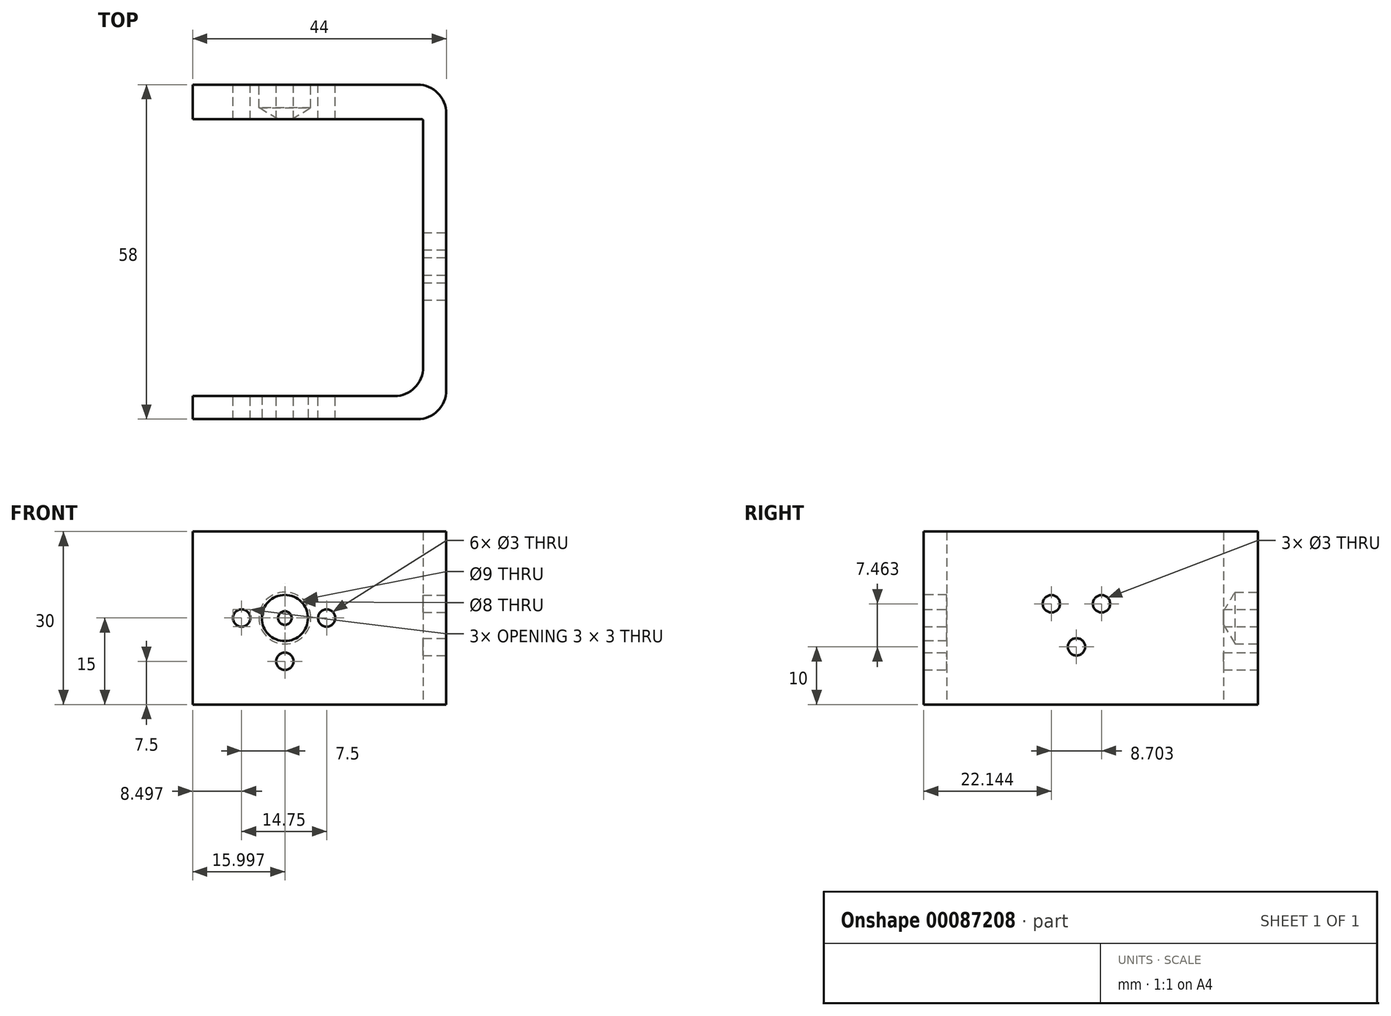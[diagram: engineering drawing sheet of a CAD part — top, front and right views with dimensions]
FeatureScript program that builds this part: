
annotation { "Feature Type Name" : "Feature", "Feature Type Description" : "" }
export const myFeature = defineFeature(function(context is Context, id is Id, definition is map)
    precondition{}
    {
        {
            var Q0;
            Q0=qCreatedBy(makeId("Top.planeOp"),FACE);
            var sketch = newSketch(context, id + "F0", { "sketchPlane" : qUnion([Q0])});
            skLineSegment(sketch, "E0", {"start": v(-0.12, 52.66) * mm, "end": v(-0.12, 9.9) * mm});
            skLineSegment(sketch, "E1", {"start": v(-5.12, 4.9) * mm, "end": v(-40.12, 4.9) * mm});
            skLineSegment(sketch, "E2", {"start": v(-0.37, 52.9) * mm, "end": v(-40.12, 52.9) * mm});
            skLineSegment(sketch, "E3", {"start": v(-40.12, 4.9) * mm, "end": v(-40.12, 0.9) * mm});
            skLineSegment(sketch, "E4", {"start": v(-40.12, 58.9) * mm, "end": v(-40.12, 52.9) * mm});
            skPoint(sketch, "E5.0.end.orphan", {"position": v(3.88, 4.9) * mm});
            skPoint(sketch, "E5.0.start.orphan", {"position": v(3.88, 54.9) * mm});
            skLineSegment(sketch, "E6", {"start": v(3.88, 53.9) * mm, "end": v(3.88, 5.9) * mm});
            skLineSegment(sketch, "E7", {"start": v(-40.12, 58.9) * mm, "end": v(-1.12, 58.9) * mm});
            skLineSegment(sketch, "E8", {"start": v(-1.12, 0.9) * mm, "end": v(-40.12, 0.9) * mm});
            skPoint(sketch, "E9.visualSharp", {"position": v(3.88, 58.9) * mm});
            skArc(sketch, "E9.filletArc", {"start": v(3.88, 53.9) * mm, "mid": v(2.41, 57.44) * mm, "end": v(-1.12, 58.9) * mm});
            skPoint(sketch, "E10.visualSharp", {"position": v(-0.12, 52.9) * mm});
            skArc(sketch, "E10.filletArc", {"start": v(-0.12, 52.66) * mm, "mid": v(-0.2, 52.83) * mm, "end": v(-0.37, 52.9) * mm});
            skPoint(sketch, "E11.visualSharp", {"position": v(-0.12, 4.9) * mm});
            skLineSegment(sketch, "E11.filletArc", {"start": v(-0.12, 4.9) * mm, "end": v(-0.12, 4.9) * mm});
            skPoint(sketch, "E12.visualSharp", {"position": v(3.88, 0.9) * mm});
            skArc(sketch, "E12.filletArc", {"start": v(-1.12, 0.9) * mm, "mid": v(2.41, 2.37) * mm, "end": v(3.88, 5.9) * mm});
            skArc(sketch, "E13.filletArc", {"start": v(-5.12, 4.9) * mm, "mid": v(-1.59, 6.37) * mm, "end": v(-0.12, 9.9) * mm});
            skSolve(sketch);
        }
        {
            var Q0;
            Q0 = qSketchRegion(id + "F0", true);
            extrude(context, id + "F1", {"entities" : qUnion([Q0]), "depth" : 30 * mm});
        }
        {
            var Q0;
            Q0=makeQuery(id+"F1.opExtrude","SWEPT_FACE",FACE,{"disambiguationData":[OSD([sQuery(id+"F0.wireOp",EDGE,"E6")])]});
            var sketch = newSketch(context, id + "F2", { "sketchPlane" : qUnion([Q0])});
            skCircle(sketch, "E14", {"center": v(23.05, 17.46) * mm, "radius": 1.5 * mm});
            skCircle(sketch, "E15", {"center": v(27.4, 10) * mm, "radius": 1.5 * mm});
            skCircle(sketch, "E16", {"center": v(31.76, 17.46) * mm, "radius": 1.5 * mm});
            skPoint(sketch, "E17.orphan", {"position": v(0.9, 15) * mm});
            skPoint(sketch, "E18.orphan", {"position": v(0.9, 0) * mm});
            skPoint(sketch, "E19.orphan", {"position": v(29.9, 0) * mm});
            skPoint(sketch, "E20.orphan", {"position": v(53.9, 15) * mm});
            skPoint(sketch, "E21.orphan", {"position": v(53.9, 30) * mm});
            skPoint(sketch, "E22.orphan", {"position": v(29.9, 30) * mm});
            skPoint(sketch, "E23.center.orphan", {"position": v(27.4, 15) * mm});
            skSolve(sketch);
        }
        {
            var Q0;
            Q0=sQuery(id+"F2.wireOp",VERTEX,"E14.center");
            var Q1;
            Q1=sQuery(id+"F2.wireOp",VERTEX,"E15.center");
            var Q2;
            Q2=sQuery(id+"F2.wireOp",VERTEX,"E16.center");
            var Q3;
            Q3=makeQuery(id+"F1.opExtrude","SWEPT_BODY",BODY,{"disambiguationData":[OSD([sQuery(id+"F0.wireOp",EDGE,"E0"),sQuery(id+"F0.wireOp",EDGE,"E1"),sQuery(id+"F0.wireOp",EDGE,"E2"),sQuery(id+"F0.wireOp",EDGE,"E3"),sQuery(id+"F0.wireOp",EDGE,"E4"),sQuery(id+"F0.wireOp",EDGE,"E6"),sQuery(id+"F0.wireOp",EDGE,"E7"),sQuery(id+"F0.wireOp",EDGE,"E8"),sQuery(id+"F0.wireOp",EDGE,"E9.filletArc"),sQuery(id+"F0.wireOp",EDGE,"E10.filletArc"),sQuery(id+"F0.wireOp",EDGE,"E11.filletArc")])]});
            hole(context, id + "F3", {"style" : HoleStyle.SIMPLE, "endStyle" : HoleEndStyle.THROUGH, "holeDiameter" : 3 * mm, "locations" : qUnion([Q0, Q1, Q2]), "scope" : qUnion([Q3]), "isTappedThrough" : true});
        }
        {
            var Q0;
            Q0=makeQuery(id+"F1.opExtrude","SWEPT_FACE",FACE,{"disambiguationData":[OSD([sQuery(id+"F0.wireOp",EDGE,"E7")])]});
            var sketch = newSketch(context, id + "F4", { "sketchPlane" : qUnion([Q0])});
            skCircle(sketch, "E24", {"center": v(24.12, 15) * mm, "radius": 4.5 * mm});
            skCircle(sketch, "E25", {"center": v(24.12, 22.5) * mm, "radius": 1.5 * mm});
            skCircle(sketch, "E26", {"center": v(16.87, 15) * mm, "radius": 1.5 * mm});
            skCircle(sketch, "E27", {"center": v(24.12, 7.5) * mm, "radius": 1.5 * mm});
            skCircle(sketch, "E28", {"center": v(31.62, 15) * mm, "radius": 1.5 * mm});
            skSolve(sketch);
        }
        {
            var Q0;
            Q0=sQuery(id+"F4.wireOp",VERTEX,"E24.center");
            var Q1;
            Q1=makeQuery(id+"F1.opExtrude","SWEPT_BODY",BODY,{"disambiguationData":[OSD([sQuery(id+"F0.wireOp",EDGE,"E0"),sQuery(id+"F0.wireOp",EDGE,"E1"),sQuery(id+"F0.wireOp",EDGE,"E2"),sQuery(id+"F0.wireOp",EDGE,"E3"),sQuery(id+"F0.wireOp",EDGE,"E4"),sQuery(id+"F0.wireOp",EDGE,"E6"),sQuery(id+"F0.wireOp",EDGE,"E7"),sQuery(id+"F0.wireOp",EDGE,"E8"),sQuery(id+"F0.wireOp",EDGE,"E9.filletArc"),sQuery(id+"F0.wireOp",EDGE,"E10.filletArc")])]});
            hole(context, id + "F5", {"style" : HoleStyle.SIMPLE, "endStyle" : HoleEndStyle.BLIND, "holeDiameter" : 9 * mm, "holeDepth" : 4 * mm, "startFromSketch" : true, "locations" : qUnion([Q0]), "scope" : qUnion([Q1])});
        }
        {
            var Q0;
            Q0=makeQuery(id+"F1.opExtrude","SWEPT_FACE",FACE,{"disambiguationData":[OSD([sQuery(id+"F0.wireOp",EDGE,"E7")])]});
            var sketch = newSketch(context, id + "F6", { "sketchPlane" : qUnion([Q0])});
            skCircle(sketch, "E29", {"center": v(24.12, 15) * mm, "radius": 4.5 * mm});
            skPoint(sketch, "E30.trimOffspring.end.orphan", {"position": v(31.62, 15) * mm});
            skPoint(sketch, "E31.start.orphan", {"position": v(24.12, 7.5) * mm});
            skPoint(sketch, "E32.orphan", {"position": v(16.87, 15) * mm});
            skSolve(sketch);
        }
        {
            var Q0;
            Q0=sQuery(id+"F6.wireOp",VERTEX,"E30.trimOffspring.end.orphan");
            var Q1;
            Q1=sQuery(id+"F6.wireOp",VERTEX,"E31.start.orphan");
            var Q2;
            Q2=sQuery(id+"F6.wireOp",VERTEX,"E32.orphan");
            var Q3;
            Q3=makeQuery(id+"F1.opExtrude","SWEPT_BODY",BODY,{"disambiguationData":[OSD([sQuery(id+"F0.wireOp",EDGE,"E0"),sQuery(id+"F0.wireOp",EDGE,"E1"),sQuery(id+"F0.wireOp",EDGE,"E2"),sQuery(id+"F0.wireOp",EDGE,"E3"),sQuery(id+"F0.wireOp",EDGE,"E4"),sQuery(id+"F0.wireOp",EDGE,"E6"),sQuery(id+"F0.wireOp",EDGE,"E7"),sQuery(id+"F0.wireOp",EDGE,"E8"),sQuery(id+"F0.wireOp",EDGE,"E9.filletArc"),sQuery(id+"F0.wireOp",EDGE,"E10.filletArc")])]});
            hole(context, id + "F7", {"style" : HoleStyle.SIMPLE, "endStyle" : HoleEndStyle.THROUGH, "holeDiameter" : 3 * mm, "startFromSketch" : true, "locations" : qUnion([Q0, Q1, Q2]), "scope" : qUnion([Q3]), "isTappedThrough" : true});
        }
        {
            var Q0;
            Q0=makeQuery(id+"F1.opExtrude","SWEPT_FACE",FACE,{"disambiguationData":[OSD([sQuery(id+"F0.wireOp",EDGE,"E8")])]});
            var sketch = newSketch(context, id + "F8", { "sketchPlane" : qUnion([Q0])});
            skLineSegment(sketch, "E33", {"start": v(-40.12, 0) * mm, "end": v(-24.12, 0) * mm});
            skPoint(sketch, "E34.orphan", {"position": v(-40.12, 15) * mm});
            skCircle(sketch, "E35", {"center": v(-24.12, 15) * mm, "radius": 5.1 * mm});
            skPoint(sketch, "E36.orphan", {"position": v(3.88, 15) * mm});
            skSolve(sketch);
        }
        {
            var Q0;
            Q0=sQuery(id+"F8.wireOp",VERTEX,"E35.center");
            var Q1;
            Q1=makeQuery(id+"F1.opExtrude","SWEPT_BODY",BODY,{"disambiguationData":[OSD([sQuery(id+"F0.wireOp",EDGE,"E0"),sQuery(id+"F0.wireOp",EDGE,"E1"),sQuery(id+"F0.wireOp",EDGE,"E2"),sQuery(id+"F0.wireOp",EDGE,"E3"),sQuery(id+"F0.wireOp",EDGE,"E4"),sQuery(id+"F0.wireOp",EDGE,"E6"),sQuery(id+"F0.wireOp",EDGE,"E7"),sQuery(id+"F0.wireOp",EDGE,"E8"),sQuery(id+"F0.wireOp",EDGE,"E9.filletArc"),sQuery(id+"F0.wireOp",EDGE,"E10.filletArc"),sQuery(id+"F0.wireOp",EDGE,"E12.filletArc"),sQuery(id+"F0.wireOp",EDGE,"E13.filletArc")])]});
            hole(context, id + "F9", {"style" : HoleStyle.SIMPLE, "endStyle" : HoleEndStyle.BLIND, "holeDiameter" : 8 * mm, "holeDepth" : 4 * mm, "startFromSketch" : true, "locations" : qUnion([Q0]), "scope" : qUnion([Q1])});
        }
    });
